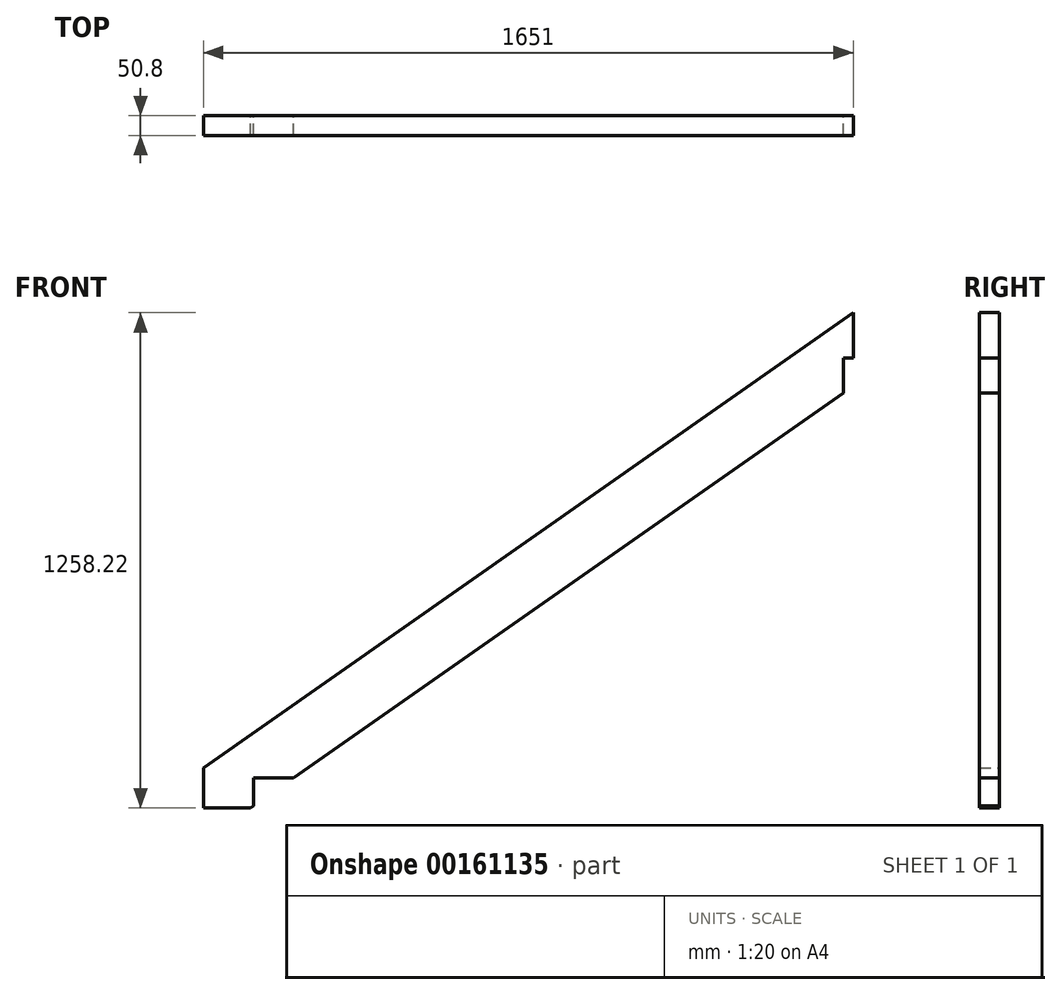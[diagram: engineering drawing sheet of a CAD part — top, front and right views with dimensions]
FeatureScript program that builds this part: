
annotation { "Feature Type Name" : "Feature", "Feature Type Description" : "" }
export const myFeature = defineFeature(function(context is Context, id is Id, definition is map)
    precondition{}
    {
        {
            var Q0;
            Q0=qCreatedBy(makeId("Front.planeOp"),FACE);
            var sketch = newSketch(context, id + "F0", { "sketchPlane" : qUnion([Q0])});
            skLineSegment(sketch, "E0", {"start": v(1524, 1043.63) * mm, "end": v(1524, 928.22) * mm});
            skPoint(sketch, "E1.orphan", {"position": v(286.12, 0) * mm});
            skLineSegment(sketch, "E2", {"start": v(0, -138.39) * mm, "end": v(0, -209.53) * mm});
            skLineSegment(sketch, "E3", {"start": v(101.6, -138.39) * mm, "end": v(101.6, -189.38) * mm, "construction": true});
            skPoint(sketch, "E4.orphan", {"position": v(101.6, 0) * mm});
            skLineSegment(sketch, "E5.bottom", {"start": v(1498.6, 928.22) * mm, "end": v(1549.4, 928.22) * mm});
            skLineSegment(sketch, "E5.top", {"start": v(1498.6, 750.42) * mm, "end": v(1549.4, 750.42) * mm, "construction": true});
            skLineSegment(sketch, "E5.left", {"start": v(1498.6, 928.22) * mm, "end": v(1498.6, 839.8) * mm});
            skLineSegment(sketch, "E5.right", {"start": v(1549.4, 928.22) * mm, "end": v(1549.4, 750.42) * mm, "construction": true});
            skLineSegment(sketch, "E6.trimOffspring", {"start": v(-7.22, -214.59) * mm, "end": v(0, -209.53) * mm});
            skLineSegment(sketch, "E7", {"start": v(0, -138.39) * mm, "end": v(101.6, -138.39) * mm});
            skLineSegment(sketch, "E8", {"start": v(101.6, -189.38) * mm, "end": v(0, -189.38) * mm, "construction": true});
            skLineSegment(sketch, "E9", {"start": v(-127, -112.41) * mm, "end": v(1524, 1043.63) * mm});
            skLineSegment(sketch, "E10", {"start": v(-127, -214.59) * mm, "end": v(-7.22, -214.59) * mm});
            skLineSegment(sketch, "E11", {"start": v(-127, -214.59) * mm, "end": v(-127, -112.41) * mm});
            skLineSegment(sketch, "E12.trimOffspring", {"start": v(101.6, -138.39) * mm, "end": v(1498.6, 839.8) * mm});
            skSolve(sketch);
        }
        {
            var Q0;
            Q0=qSketchRegion(id+"F0",true);
            extrude(context, id + "F1", {"entities" : qUnion([Q0]), "depth" : 50.8 * mm});
        }
    });
